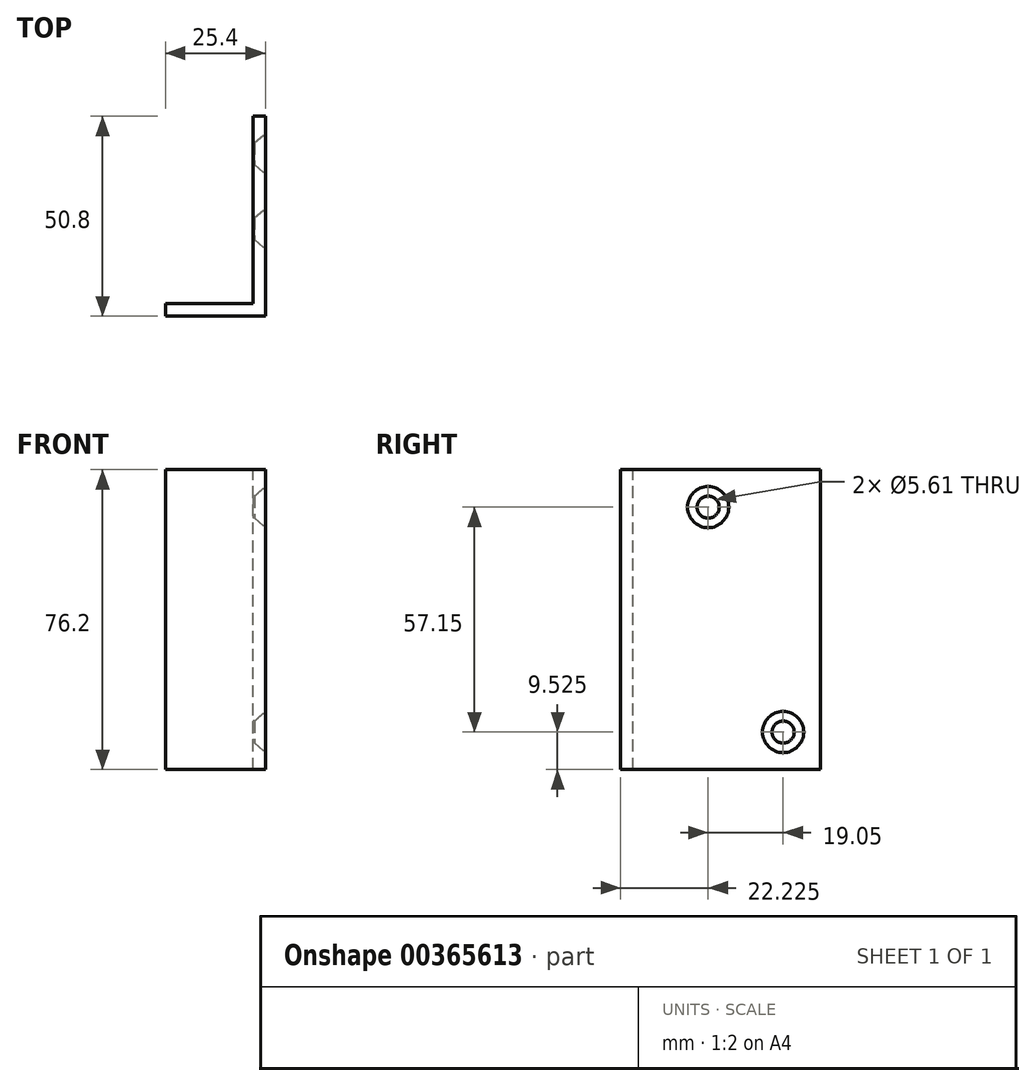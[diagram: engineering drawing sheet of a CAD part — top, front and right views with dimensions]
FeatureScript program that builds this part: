
annotation { "Feature Type Name" : "Feature", "Feature Type Description" : "" }
export const myFeature = defineFeature(function(context is Context, id is Id, definition is map)
    precondition{}
    {
        {
            var Q0;
            Q0=qCreatedBy(makeId("Right.planeOp"),FACE);
            var sketch = newSketch(context, id + "F0", { "sketchPlane" : qUnion([Q0])});
            skLineSegment(sketch, "E0.bottom", {"start": v(25.4, -38.1) * mm, "end": v(-25.4, -38.1) * mm});
            skLineSegment(sketch, "E0.top", {"start": v(25.4, 38.1) * mm, "end": v(-25.4, 38.1) * mm});
            skLineSegment(sketch, "E0.left", {"start": v(25.4, -38.1) * mm, "end": v(25.4, 38.1) * mm});
            skLineSegment(sketch, "E0.right", {"start": v(-25.4, -38.1) * mm, "end": v(-25.4, 38.1) * mm});
            skPoint(sketch, "E0.middle", {"position": v(0, 0) * mm});
            skSolve(sketch);
        }
        {
            var Q0;
            Q0=qSketchRegion(id+"F0",true);
            extrude(context, id + "F1", {"entities" : qUnion([Q0]), "depth" : 25.4 * mm, "offsetDistance" : 25.4 * mm});
        }
        {
            var Q0;
            Q0=makeQuery(id+"F1.opExtrude","CAP_FACE",FACE,{"disambiguationData":[OSD([sQuery(id+"F0.wireOp",EDGE,"E0.bottom"),sQuery(id+"F0.wireOp",EDGE,"E0.top"),sQuery(id+"F0.wireOp",EDGE,"E0.left"),sQuery(id+"F0.wireOp",EDGE,"E0.right")])],"isStart":false});
            var sketch = newSketch(context, id + "F2", { "sketchPlane" : qUnion([Q0])});
            skPoint(sketch, "E1", {"position": v(-3.18, 28.58) * mm});
            skPoint(sketch, "E2", {"position": v(15.88, -28.58) * mm});
            skSolve(sketch);
        }
        {
            var Q0;
            Q0=sQuery(id+"F2.wireOp",VERTEX,"E1");
            var Q1;
            Q1=sQuery(id+"F2.wireOp",VERTEX,"9c431e09-931f-43e2-840f-4f00e6efbce6");
            var Q2;
            Q2=sQuery(id+"F2.wireOp",VERTEX,"E2");
            var Q3;
            Q3=sQuery(id+"F2.wireOp",VERTEX,"9e30ab42-1027-4ecf-a6f1-ec90ac2d1b19");
            var Q4;
            Q4=makeQuery(id+"F1.opExtrude","SWEPT_BODY",BODY,{"disambiguationData":[OSD([sQuery(id+"F0.wireOp",EDGE,"E0.bottom"),sQuery(id+"F0.wireOp",EDGE,"E0.top"),sQuery(id+"F0.wireOp",EDGE,"E0.left"),sQuery(id+"F0.wireOp",EDGE,"E0.right")])]});
            hole(context, id + "F3", {"style" : HoleStyle.C_SINK, "endStyle" : HoleEndStyle.THROUGH, "standardTappedOrClearance" : lookupTablePath({ "fit" : "Normal (ASME)", "standard" : "ANSI", "size" : "#10", "type" : "Clearance" }), "standardBlindInLast" : lookupTablePath({ "fit" : "Normal", "standard" : "ANSI", "engagement" : "75%", "pitch" : "24 tpi", "size" : "#10", "type" : "Clearance & tapped" }), "holeDiameter" : 5.61 * mm, "cSinkDiameter" : 10.44 * mm, "cSinkAngle" : 82 * degree, "majorDiameter" : 6.35 * mm, "isTappedThrough" : true, "tappedDepth" : 12.7 * mm, "tapClearance" : 3, "locations" : qUnion([Q0, Q1, Q2, Q3]), "scope" : qUnion([Q4]), "startStyle" : HoleStartStyle.SKETCH});
        }
        {
            var Q0;
            Q0=makeQuery(id+"F1.opExtrude","SWEPT_FACE",FACE,{"disambiguationData":[OSD([sQuery(id+"F0.wireOp",EDGE,"E0.top")])]});
            var sketch = newSketch(context, id + "F4", { "sketchPlane" : qUnion([Q0])});
            skLineSegment(sketch, "E3.bottom", {"start": v(0, 25.4) * mm, "end": v(22.23, 25.4) * mm});
            skLineSegment(sketch, "E3.top", {"start": v(0, -22.23) * mm, "end": v(22.23, -22.23) * mm});
            skLineSegment(sketch, "E3.left", {"start": v(0, 25.4) * mm, "end": v(0, -22.23) * mm});
            skLineSegment(sketch, "E3.right", {"start": v(22.23, 25.4) * mm, "end": v(22.23, -22.23) * mm});
            skSolve(sketch);
        }
        {
            var Q0;
            Q0 = qSketchRegion(id + "F4", true);
            extrude(context, id + "F5", {"entities" : qUnion([Q0]), "operationType" : NewBodyOperationType.REMOVE, "endBound" : BoundingType.THROUGH_ALL, "oppositeDirection" : true, "depth" : 25.4 * mm, "offsetDistance" : 25.4 * mm});
        }
    });
